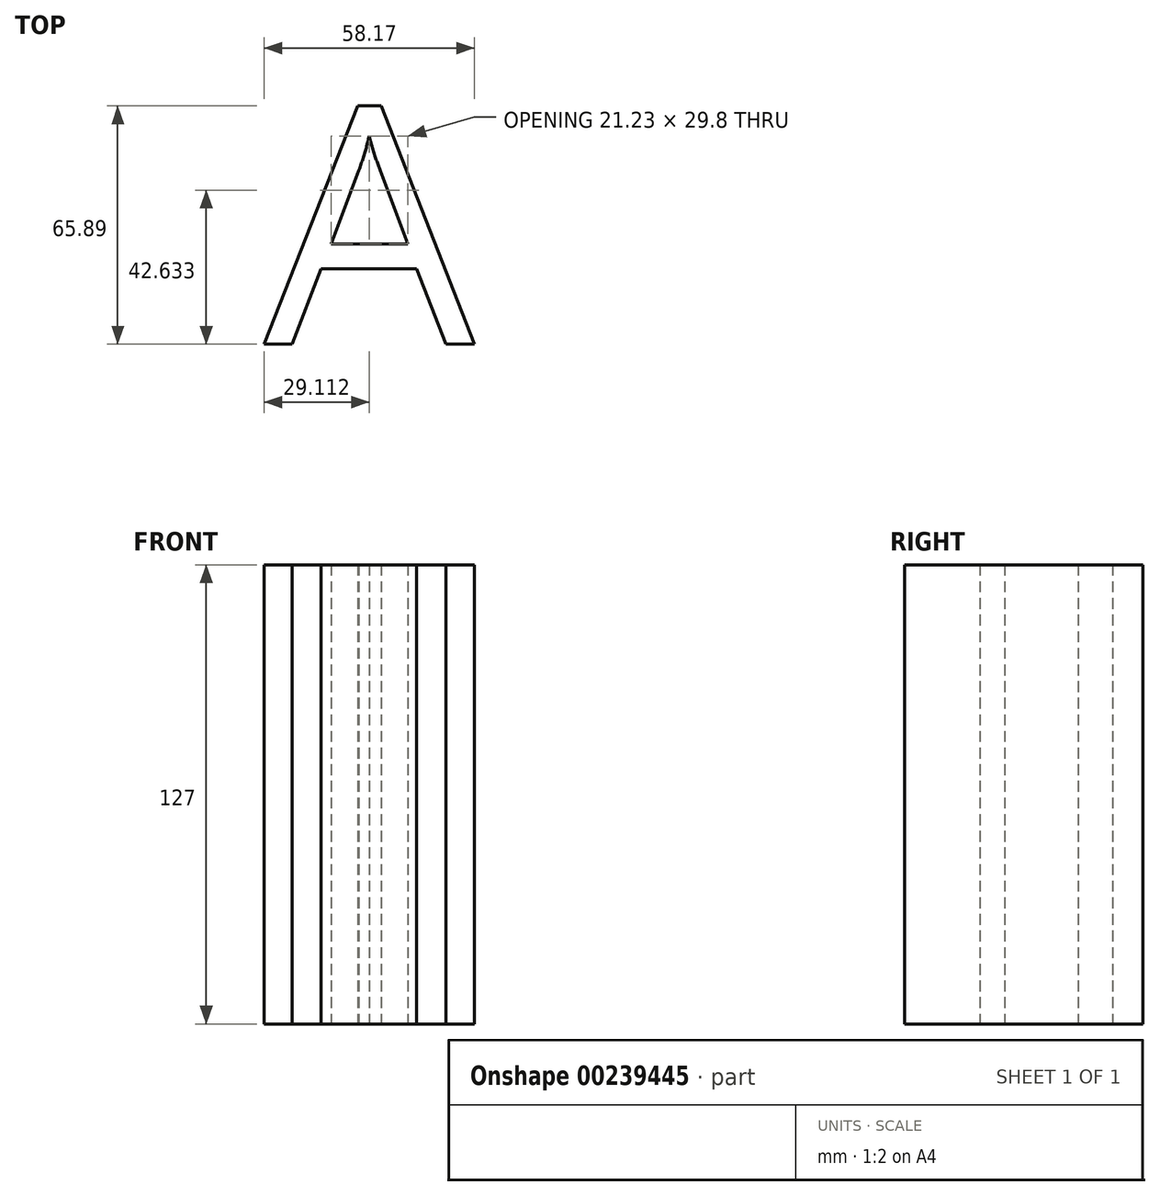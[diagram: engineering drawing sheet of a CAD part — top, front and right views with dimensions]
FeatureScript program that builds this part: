
annotation { "Feature Type Name" : "Feature", "Feature Type Description" : "" }
export const myFeature = defineFeature(function(context is Context, id is Id, definition is map)
    precondition{}
    {
        {
            var Q0;
            Q0=qCreatedBy(makeId("Top.planeOp"),FACE);
            var sketch = newSketch(context, id + "F0", { "sketchPlane" : qUnion([Q0])});
            skText(sketch, "E0", { "text": "A\n", "fontName": "OpenSans-Regular.ttf"});
            const initialGuessF0  = {"E0": [-0.02738, -0.02296, 1, 0, 0.06618]};
            skSetInitialGuess(sketch, initialGuessF0);
            skSolve(sketch);
        }
        {
            var Q0;
            Q0 = qSketchRegion(id + "F0", true);
            extrude(context, id + "F1", {"entities" : qUnion([Q0]), "depth" : 127 * mm});
        }
    });
